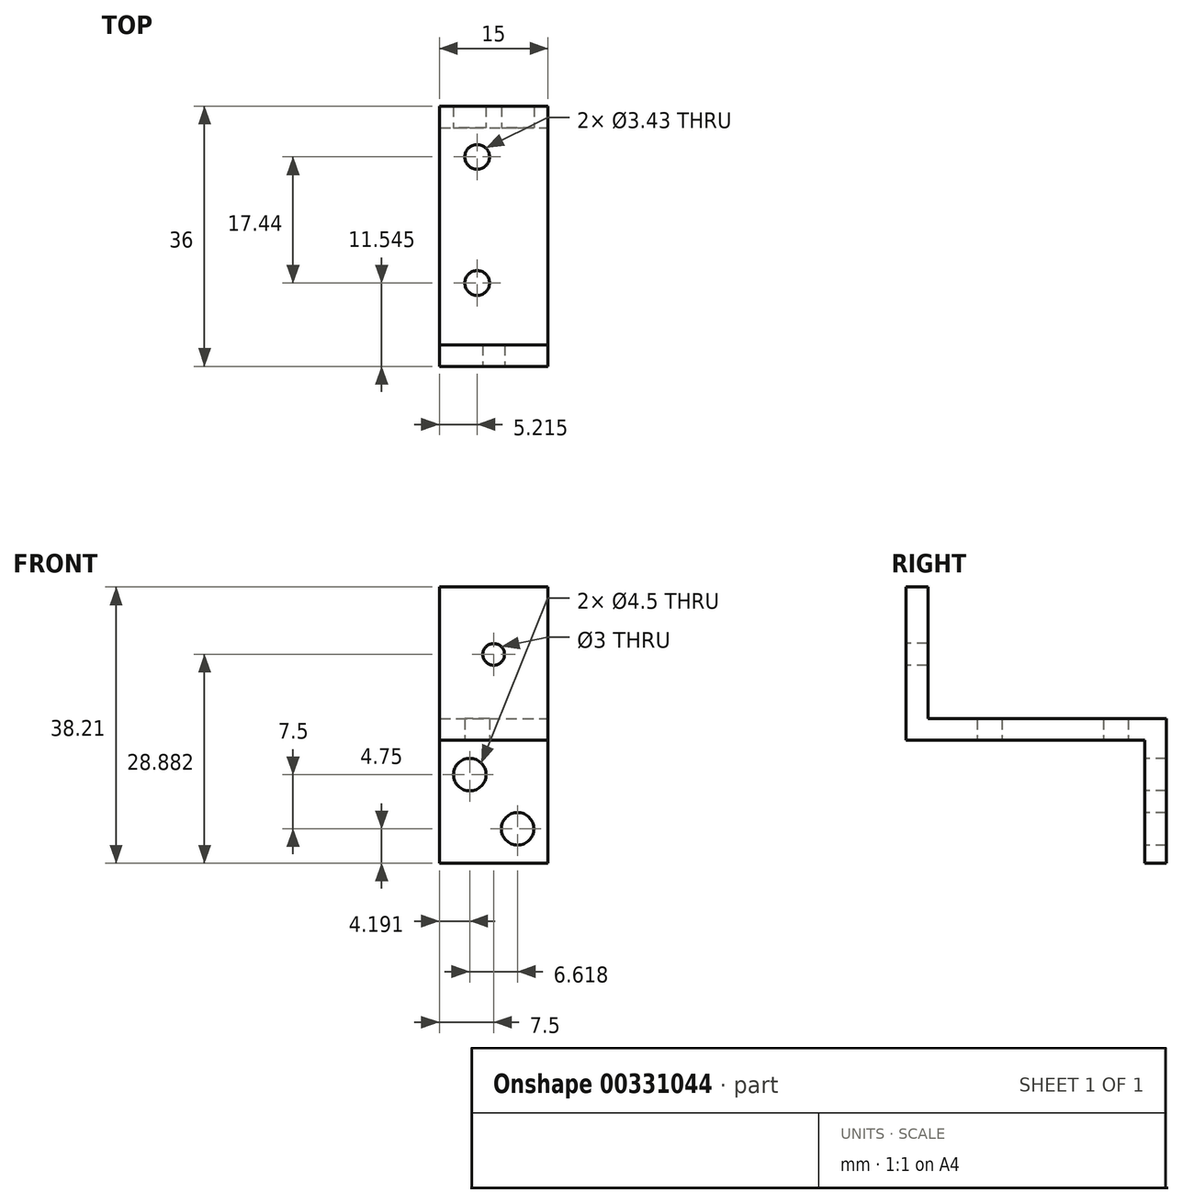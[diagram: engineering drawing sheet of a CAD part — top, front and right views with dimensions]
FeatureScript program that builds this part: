
annotation { "Feature Type Name" : "Feature", "Feature Type Description" : "" }
export const myFeature = defineFeature(function(context is Context, id is Id, definition is map)
    precondition{}
    {
        {
            var Q0;
            Q0=qCreatedBy(makeId("Top.planeOp"),FACE);
            var sketch = newSketch(context, id + "F0", { "sketchPlane" : qUnion([Q0])});
            skLineSegment(sketch, "E0.bottom", {"start": v(-7.5, 16.5) * mm, "end": v(7.5, 16.5) * mm});
            skLineSegment(sketch, "E0.top", {"start": v(-7.5, -16.5) * mm, "end": v(7.5, -16.5) * mm});
            skLineSegment(sketch, "E0.left", {"start": v(-7.5, 16.5) * mm, "end": v(-7.5, -16.5) * mm});
            skLineSegment(sketch, "E0.right", {"start": v(7.5, 16.5) * mm, "end": v(7.5, -16.5) * mm});
            skPoint(sketch, "E0.middle", {"position": v(0, 0) * mm});
            skCircle(sketch, "E1", {"center": v(-2.28, 12.48) * mm, "radius": 1.72 * mm});
            skCircle(sketch, "E2", {"center": v(-2.28, -4.96) * mm, "radius": 1.72 * mm});
            skLineSegment(sketch, "E3", {"start": v(-2.28, 12.48) * mm, "end": v(-2.28, -7.08) * mm, "construction": true});
            skSolve(sketch);
        }
        {
            var Q0;
            Q0 = qSketchRegion(id + "F0", true);
            extrude(context, id + "F1", {"entities" : qUnion([Q0]), "depth" : 3 * mm});
        }
        {
            var Q0;
            Q0=makeQuery(id+"F1.opExtrude","SWEPT_FACE",FACE,{"disambiguationData":[OSD([sQuery(id+"F0.wireOp",EDGE,"E0.bottom")])]});
            var sketch = newSketch(context, id + "F2", { "sketchPlane" : qUnion([Q0])});
            skLineSegment(sketch, "E4", {"start": v(7.5, 3) * mm, "end": v(7.5, -17) * mm});
            skLineSegment(sketch, "E5", {"start": v(7.5, 3) * mm, "end": v(-7.5, 3) * mm});
            skLineSegment(sketch, "E6", {"start": v(-7.5, 3) * mm, "end": v(-7.5, -17) * mm});
            skLineSegment(sketch, "E7", {"start": v(-7.5, -17) * mm, "end": v(7.5, -17) * mm});
            skLineSegment(sketch, "E8", {"start": v(7.5, 0) * mm, "end": v(-7.5, -17) * mm, "construction": true});
            skCircle(sketch, "E9", {"center": v(-3.3, -12.25) * mm, "radius": 2.25 * mm});
            skLineSegment(sketch, "E10", {"start": v(7.5, -17) * mm, "end": v(-7.5, 0) * mm, "construction": true});
            skCircle(sketch, "E11", {"center": v(3.3, -4.75) * mm, "radius": 2.25 * mm});
            skSolve(sketch);
        }
        {
            var Q0;
            Q0 = qSketchRegion(id + "F2", true);
            extrude(context, id + "F3", {"entities" : qUnion([Q0]), "operationType" : NewBodyOperationType.ADD, "depth" : 3 * mm});
        }
        {
            var Q0;
            Q0=makeQuery(id+"F1.opExtrude","SWEPT_FACE",FACE,{"disambiguationData":[OSD([sQuery(id+"F0.wireOp",EDGE,"E0.top")])]});
            var sketch = newSketch(context, id + "F4", { "sketchPlane" : qUnion([Q0])});
            skLineSegment(sketch, "E12", {"start": v(-7.5, 0) * mm, "end": v(-7.5, 21.2) * mm});
            skLineSegment(sketch, "E13", {"start": v(-7.5, 0) * mm, "end": v(7.5, 0) * mm});
            skLineSegment(sketch, "E14", {"start": v(7.5, 0) * mm, "end": v(7.5, 21.2) * mm});
            skLineSegment(sketch, "E15", {"start": v(-7.5, 21.2) * mm, "end": v(7.5, 21.2) * mm});
            skCircle(sketch, "E16", {"center": v(0, 11.88) * mm, "radius": 1.5 * mm});
            skSolve(sketch);
        }
        {
            var Q0;
            {var subQ2=sQuery(id+"F4.wireOp",EDGE,"E15");Q0=makeQuery(id+"F4.imprint","IMPRINT",FACE,{"disambiguationData":[TD([[makeQuery(id+"F4.imprint","IMPRINT",EDGE,{"derivedFrom":subQ2}),-1.0]])]});}
            extrude(context, id + "F5", {"entities" : qUnion([Q0]), "operationType" : NewBodyOperationType.ADD, "oppositeDirection" : true, "depth" : 3 * mm});
        }
    });
